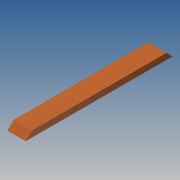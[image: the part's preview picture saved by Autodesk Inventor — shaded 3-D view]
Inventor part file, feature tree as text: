
AUTODESK INVENTOR PART (.ipt)
format: ipt  version: 2014 SP1 (Build 180222100, 222)  size: 87,552 bytes
history: native  units: in
note: dims shown in document units (in); Inventor stores cm internally (conversion verified against a paired STEP export)
features: extrude x2, sketch x2
ambient origin geometry x8: Origin, YZ Plane, XZ Plane, XY Plane, X Axis, Y Axis, Z Axis, Center Point
bodies: Solid1 (feature_tree)
feature tree (4):
  extrude  "Extrusion1"  Depth=1.4961in
  extrude  "Extrusion3"  TaperAngle=45.0deg  [1 undecoded]
  sketch  "Sketch1"  dims[d0=4.4882in d1=1.4961in]
  sketch  "Sketch7"  dims[d2=36.0in d3=0.0in d20=45.0deg d21=135.0deg d22=10.0in d23=0.0in]
note: 1 required parameter value undecoded (feature->parameter linkage not recoverable at this tier; creation-order binding heuristic only, values carry confidence <= 0.55)
